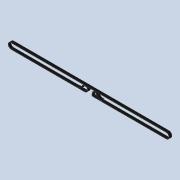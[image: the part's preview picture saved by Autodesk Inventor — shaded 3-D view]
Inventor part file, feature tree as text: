
AUTODESK INVENTOR PART (.ipt)
format: ipt  version: 2020 (Build 240168000, 168)  size: 205,312 bytes
history: native  units: mm
features: sketch x6, other x3, extrude x2, sweep x2, projected_geometry x2, reference x1
ambient origin geometry x8: Origin, YZ Plane, XZ Plane, XY Plane, X Axis, Y Axis, Z Axis, Center Point
bodies: Solid1 (feature_tree), Solid4 (feature_tree), Solid5 (feature_tree)
feature tree (16):
  extrude  "Extrusion1"  Depth=12.0mm
  extrude  "Extrusion2"  Depth=6.0mm TaperAngle=0.0deg
  sweep  "Sweep3"
  sweep  "Sweep4"
  sketch  "Sketch1"  dims[d0=355.0mm d1=12.0mm]
  sketch  "Sketch2"  dims[d2=1.0mm d3=6.0mm d4=0.0mm]
  reference  "Reference1"
  sketch  "Sketch7"  dims[d5=6.75mm d6=0.0mm d11=20.0mm]
  sketch  "Sketch8"  dims[d12=0.0mm d13=0.0mm d14=0.0mm d15=0.0mm]
  projected_geometry  "Projected Loop3"
  sketch  "Sketch9"
  sketch  "Sketch10"
  projected_geometry  "Projected Loop4"
  parser-record x1  (decoder bookkeeping rows leaked as tree rows — omitted from the tree; the rows remain in map.json)
  other  "0005-00-00 Ansamblu_General.iam"
  other  "0005-10-012.ipt:29"
note: 1 file-system path scrubbed to <path> (originals preserved in map.json)
